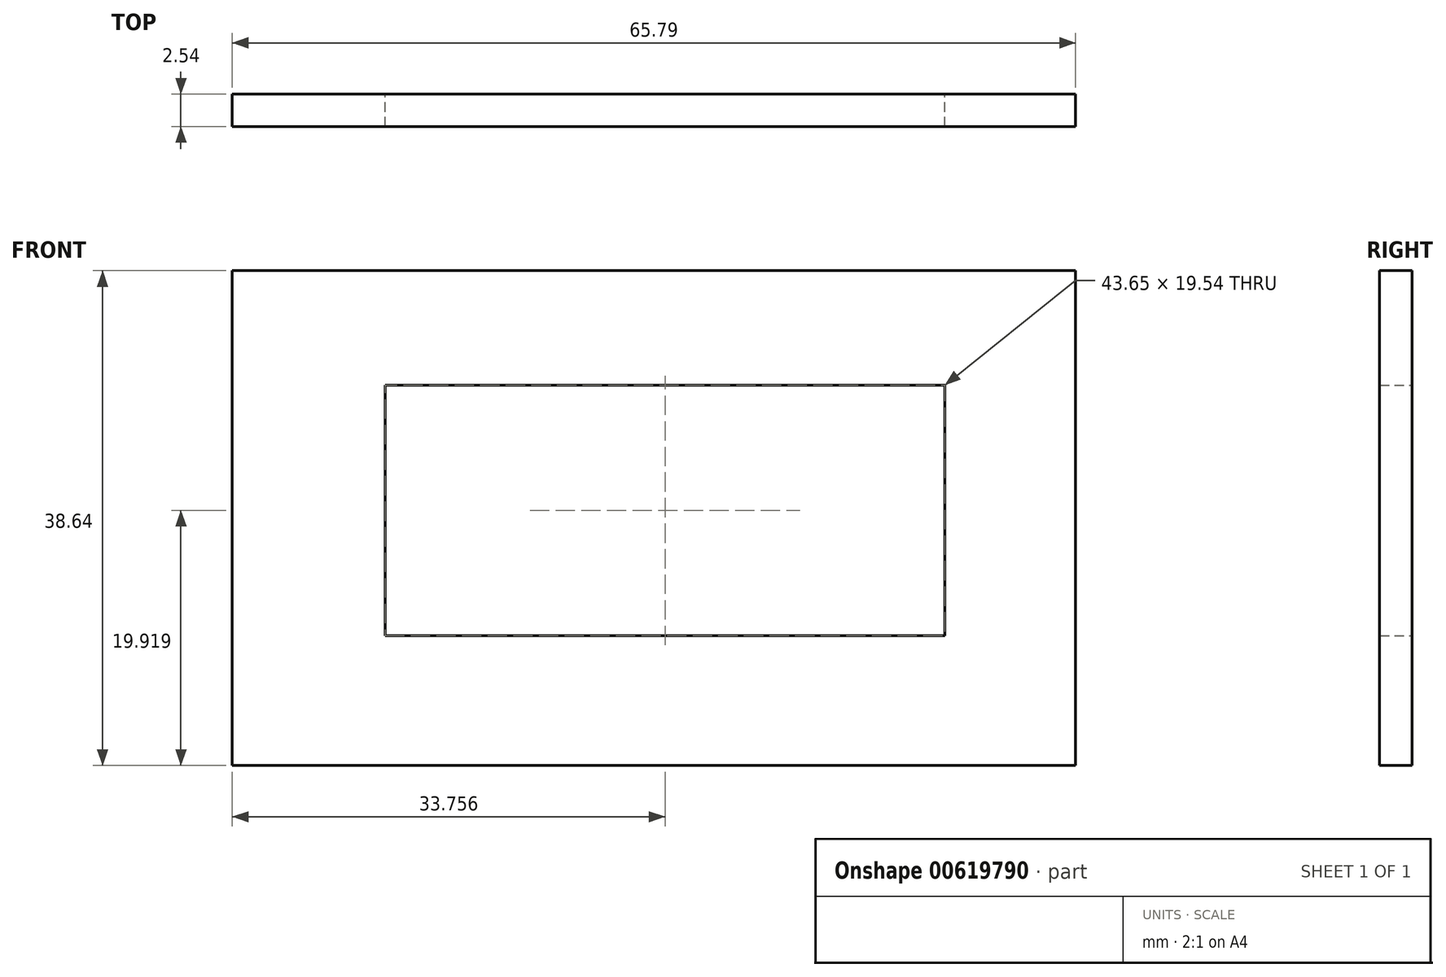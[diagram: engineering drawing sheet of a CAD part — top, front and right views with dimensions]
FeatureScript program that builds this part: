
annotation { "Feature Type Name" : "Feature", "Feature Type Description" : "" }
export const myFeature = defineFeature(function(context is Context, id is Id, definition is map)
    precondition{}
    {
        {
            var Q0;
            Q0=qCreatedBy(makeId("Front.planeOp"),FACE);
            var sketch = newSketch(context, id + "F0", { "sketchPlane" : qUnion([Q0])});
            skLineSegment(sketch, "E0.bottom", {"start": v(-34.13, 0) * mm, "end": v(31.66, 0) * mm});
            skLineSegment(sketch, "E0.top", {"start": v(-34.13, 38.64) * mm, "end": v(31.66, 38.64) * mm});
            skLineSegment(sketch, "E0.left", {"start": v(-34.13, 0) * mm, "end": v(-34.13, 38.64) * mm});
            skLineSegment(sketch, "E0.right", {"start": v(31.66, 0) * mm, "end": v(31.66, 38.64) * mm});
            skLineSegment(sketch, "E1.bottom", {"start": v(-34.13, 7.63) * mm, "end": v(31.66, 7.63) * mm});
            skLineSegment(sketch, "E1.top", {"start": v(-34.13, 4.66) * mm, "end": v(31.66, 4.66) * mm});
            skLineSegment(sketch, "E1.left", {"start": v(-34.13, 7.63) * mm, "end": v(-34.13, 4.66) * mm});
            skLineSegment(sketch, "E1.right", {"start": v(31.66, 7.63) * mm, "end": v(31.66, 4.66) * mm});
            skLineSegment(sketch, "E2.left", {"start": v(-28.08, 8.1) * mm, "end": v(-28.08, 7.63) * mm});
            skLineSegment(sketch, "E3.bottom", {"start": v(-23.87, 10.15) * mm, "end": v(23.03, 10.15) * mm});
            skLineSegment(sketch, "E3.top", {"start": v(-23.87, 33.38) * mm, "end": v(23.03, 33.38) * mm});
            skLineSegment(sketch, "E3.left", {"start": v(-23.87, 10.15) * mm, "end": v(-23.87, 33.38) * mm});
            skLineSegment(sketch, "E3.right", {"start": v(23.03, 10.15) * mm, "end": v(23.03, 33.38) * mm});
            skLineSegment(sketch, "E4.bottom", {"start": v(-22.2, 10.15) * mm, "end": v(21.45, 10.15) * mm});
            skLineSegment(sketch, "E4.top", {"start": v(-22.2, 29.69) * mm, "end": v(21.45, 29.69) * mm});
            skLineSegment(sketch, "E4.left", {"start": v(-22.2, 10.15) * mm, "end": v(-22.2, 29.69) * mm});
            skLineSegment(sketch, "E4.right", {"start": v(21.45, 10.15) * mm, "end": v(21.45, 29.69) * mm});
            skLineSegment(sketch, "E5", {"start": v(-24.98, 35.26) * mm, "end": v(-24.98, 8.12) * mm});
            skLineSegment(sketch, "E6", {"start": v(-28.08, 8.1) * mm, "end": v(-24.98, 8.12) * mm});
            skLineSegment(sketch, "E7", {"start": v(-24.98, 8.12) * mm, "end": v(27.5, 8.12) * mm});
            skLineSegment(sketch, "E8", {"start": v(27.5, 8.12) * mm, "end": v(27.5, 7.63) * mm});
            skLineSegment(sketch, "E9", {"start": v(-24.98, 35.26) * mm, "end": v(24.21, 35.26) * mm});
            skLineSegment(sketch, "E10", {"start": v(24.21, 35.26) * mm, "end": v(24.21, 8.12) * mm});
            skSolve(sketch);
        }
        {
            var Q0;
            {var subQ2=sQuery(id+"F0.wireOp",EDGE,"E0.top");Q0=makeQuery(id+"F0.imprint","IMPRINT",FACE,{"disambiguationData":[TD([[makeQuery(id+"F0.imprint","IMPRINT",EDGE,{"derivedFrom":subQ2}),-1.0]])]});}
            var Q1;
            {var subQ3=sQuery(id+"F0.wireOp",EDGE,"E2.left");Q1=makeQuery(id+"F0.imprint","IMPRINT",FACE,{"disambiguationData":[TD([[makeQuery(id+"F0.imprint","IMPRINT",EDGE,{"derivedFrom":subQ3}),1.0]])]});}
            var Q2;
            {var subQ0=sQuery(id+"F0.wireOp",EDGE,"E0.bottom");Q2=makeQuery(id+"F0.imprint","IMPRINT",FACE,{"disambiguationData":[TD([[makeQuery(id+"F0.imprint","IMPRINT",EDGE,{"derivedFrom":subQ0}),1.0]])]});}
            var Q3;
            Q3=makeQuery(id+"F0.imprint","IMPRINT",FACE,{"disambiguationData":[TD([[makeQuery(id+"F0.imprint","IMPRINT",EDGE,{"derivedFrom":sQuery(id+"F0.wireOp",EDGE,"E3.top")}),-1.0]])]});
            var Q4;
            Q4=makeQuery(id+"F0.imprint","IMPRINT",FACE,{"disambiguationData":[TD([[makeQuery(id+"F0.imprint","IMPRINT",EDGE,{"derivedFrom":sQuery(id+"F0.wireOp",EDGE,"E3.top")}),1.0]])]});
            var Q5;
            Q5=makeQuery(id+"F0.imprint","IMPRINT",FACE,{"disambiguationData":[TD([[makeQuery(id+"F0.imprint","IMPRINT",EDGE,{"derivedFrom":sQuery(id+"F0.wireOp",EDGE,"E4.bottom")}),1.0]])]});
            var Q6;
            Q6=makeQuery(id+"F0.imprint","IMPRINT",FACE,{"disambiguationData":[TD([[makeQuery(id+"F0.imprint","IMPRINT",EDGE,{"derivedFrom":sQuery(id+"F0.wireOp",EDGE,"E1.top")}),1.0]])]});
            extrude(context, id + "F1", {"entities" : qUnion([Q0, Q1, Q2, Q3, Q4, Q5, Q6]), "depth" : 2.54 * mm, "offsetDistance" : 25.4 * mm});
        }
    });
